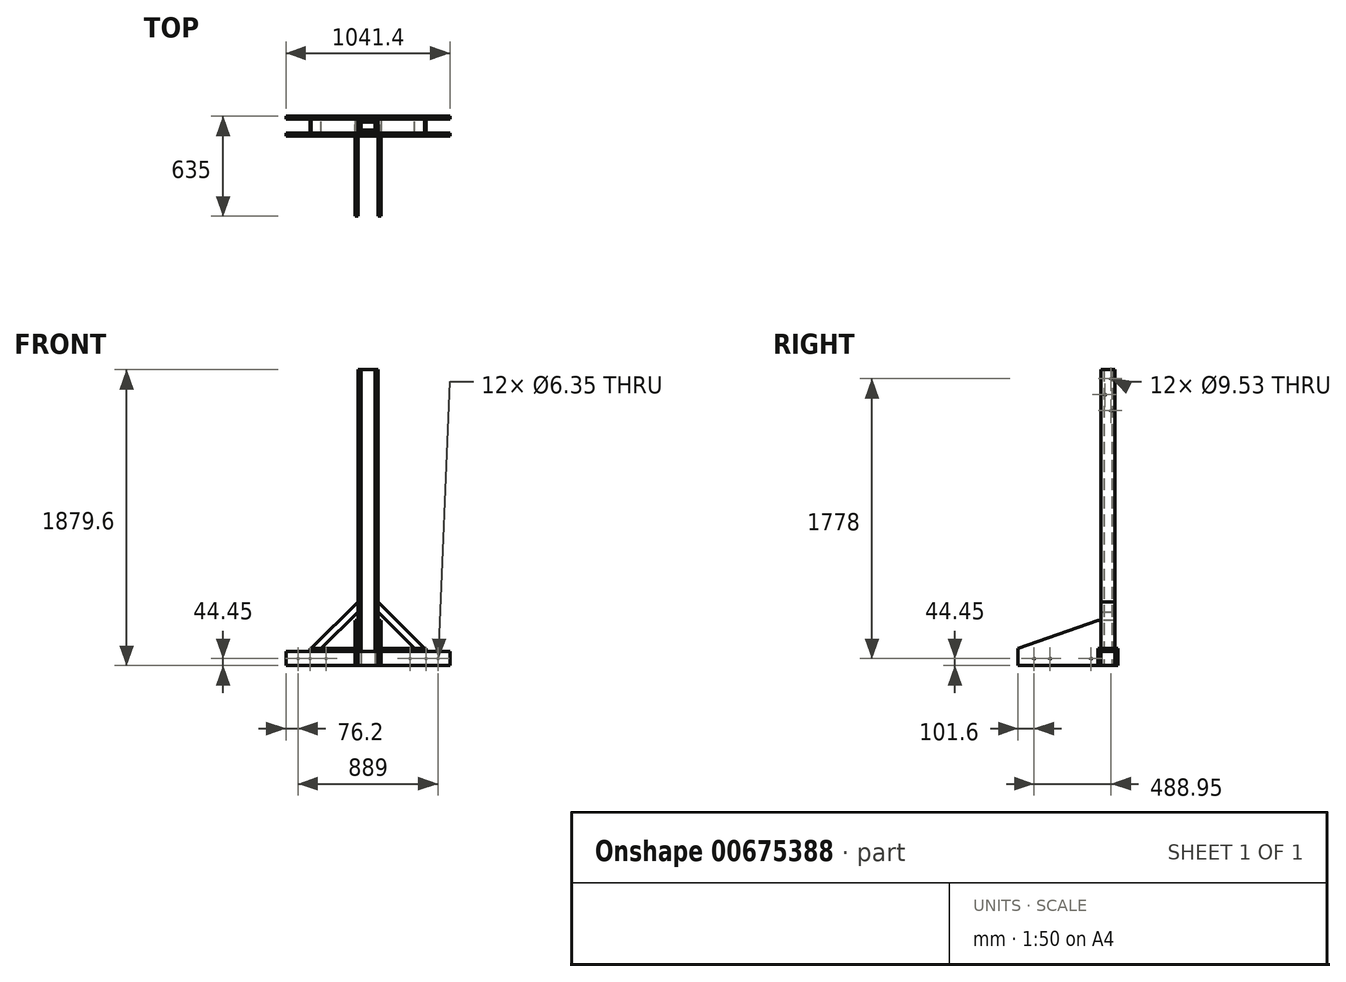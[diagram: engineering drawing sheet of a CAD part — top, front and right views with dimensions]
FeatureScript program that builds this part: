
annotation { "Feature Type Name" : "Feature", "Feature Type Description" : "" }
export const myFeature = defineFeature(function(context is Context, id is Id, definition is map)
    precondition{}
    {
        {
            var Q0;
            Q0=qCreatedBy(makeId("Top.planeOp"),FACE);
            var sketch = newSketch(context, id + "F0", { "sketchPlane" : qUnion([Q0])});
            skLineSegment(sketch, "E0.bottom", {"start": v(-44.45, 25.4) * mm, "end": v(44.45, 25.4) * mm});
            skLineSegment(sketch, "E0.top", {"start": v(-44.45, 44.45) * mm, "end": v(44.45, 44.45) * mm});
            skLineSegment(sketch, "E0.left", {"start": v(-44.45, 25.4) * mm, "end": v(-44.45, 44.45) * mm});
            skLineSegment(sketch, "E0.right", {"start": v(44.45, 25.4) * mm, "end": v(44.45, 44.45) * mm});
            skLineSegment(sketch, "E1.bottom", {"start": v(-44.45, -44.45) * mm, "end": v(44.45, -44.45) * mm});
            skLineSegment(sketch, "E1.top", {"start": v(-44.45, -25.4) * mm, "end": v(44.45, -25.4) * mm});
            skLineSegment(sketch, "E1.left", {"start": v(-44.45, -44.45) * mm, "end": v(-44.45, -25.4) * mm});
            skLineSegment(sketch, "E1.right", {"start": v(44.45, -44.45) * mm, "end": v(44.45, -25.4) * mm});
            skSolve(sketch);
        }
        {
            var Q0;
            Q0 = qSketchRegion(id + "F0", true);
            extrude(context, id + "F1", {"entities" : qUnion([Q0]), "depth" : 1879.6 * mm, "offsetDistance" : 25.4 * mm});
        }
        {
            var Q0;
            Q0=qCreatedBy(makeId("Top.planeOp"),FACE);
            var sketch = newSketch(context, id + "F2", { "sketchPlane" : qUnion([Q0])});
            skLineSegment(sketch, "E2.bottom", {"start": v(44.45, 44.45) * mm, "end": v(63.5, 44.45) * mm});
            skLineSegment(sketch, "E2.top", {"start": v(44.45, -44.45) * mm, "end": v(63.5, -44.45) * mm});
            skLineSegment(sketch, "E2.left", {"start": v(44.45, 44.45) * mm, "end": v(44.45, -44.45) * mm});
            skLineSegment(sketch, "E2.right", {"start": v(63.5, 44.45) * mm, "end": v(63.5, -44.45) * mm});
            skLineSegment(sketch, "E3.bottom", {"start": v(-44.45, -44.45) * mm, "end": v(-63.5, -44.45) * mm});
            skLineSegment(sketch, "E3.top", {"start": v(-44.45, 44.45) * mm, "end": v(-63.5, 44.45) * mm});
            skLineSegment(sketch, "E3.left", {"start": v(-44.45, -44.45) * mm, "end": v(-44.45, 44.45) * mm});
            skLineSegment(sketch, "E3.right", {"start": v(-63.5, -44.45) * mm, "end": v(-63.5, 44.45) * mm});
            skSolve(sketch);
        }
        {
            var Q0;
            Q0 = qSketchRegion(id + "F2", true);
            extrude(context, id + "F3", {"entities" : qUnion([Q0]), "depth" : 1879.6 * mm, "offsetDistance" : 25.4 * mm});
        }
        {
            var Q0;
            Q0=qCreatedBy(makeId("Top.planeOp"),FACE);
            var sketch = newSketch(context, id + "F4", { "sketchPlane" : qUnion([Q0])});
            skLineSegment(sketch, "E4.bottom", {"start": v(-520.7, 44.45) * mm, "end": v(520.7, 44.45) * mm});
            skLineSegment(sketch, "E4.top", {"start": v(-520.7, 63.5) * mm, "end": v(520.7, 63.5) * mm});
            skLineSegment(sketch, "E4.left", {"start": v(-520.7, 44.45) * mm, "end": v(-520.7, 63.5) * mm});
            skLineSegment(sketch, "E4.right", {"start": v(520.7, 44.45) * mm, "end": v(520.7, 63.5) * mm});
            skLineSegment(sketch, "E5.bottom", {"start": v(-520.7, -63.5) * mm, "end": v(520.7, -63.5) * mm});
            skLineSegment(sketch, "E5.top", {"start": v(-520.7, -44.45) * mm, "end": v(520.7, -44.45) * mm});
            skLineSegment(sketch, "E5.left", {"start": v(-520.7, -63.5) * mm, "end": v(-520.7, -44.45) * mm});
            skLineSegment(sketch, "E5.right", {"start": v(520.7, -63.5) * mm, "end": v(520.7, -44.45) * mm});
            skSolve(sketch);
        }
        {
            var Q0;
            Q0 = qSketchRegion(id + "F4", true);
            extrude(context, id + "F5", {"entities" : qUnion([Q0]), "depth" : 88.9 * mm, "offsetDistance" : 25.4 * mm});
        }
        {
            var Q0;
            Q0=makeQuery(id+"F5.opExtrude","CAP_FACE",FACE,{"disambiguationData":[OSD([sQuery(id+"F4.wireOp",EDGE,"E4.bottom"),sQuery(id+"F4.wireOp",EDGE,"E4.top"),sQuery(id+"F4.wireOp",EDGE,"E4.left"),sQuery(id+"F4.wireOp",EDGE,"E4.right")])],"isStart":false});
            var sketch = newSketch(context, id + "F6", { "sketchPlane" : qUnion([Q0])});
            skLineSegment(sketch, "E6.bottom", {"start": v(-63.5, 63.5) * mm, "end": v(-368.3, 63.5) * mm});
            skLineSegment(sketch, "E6.top", {"start": v(-63.5, -63.5) * mm, "end": v(-368.3, -63.5) * mm});
            skLineSegment(sketch, "E6.left", {"start": v(-63.5, 63.5) * mm, "end": v(-63.5, -63.5) * mm});
            skLineSegment(sketch, "E6.right", {"start": v(-368.3, 63.5) * mm, "end": v(-368.3, -63.5) * mm});
            skLineSegment(sketch, "E7.bottom", {"start": v(63.5, 63.5) * mm, "end": v(368.3, 63.5) * mm});
            skLineSegment(sketch, "E7.top", {"start": v(63.5, -63.5) * mm, "end": v(368.3, -63.5) * mm});
            skLineSegment(sketch, "E7.left", {"start": v(63.5, 63.5) * mm, "end": v(63.5, -63.5) * mm});
            skLineSegment(sketch, "E7.right", {"start": v(368.3, 63.5) * mm, "end": v(368.3, -63.5) * mm});
            skSolve(sketch);
        }
        {
            var Q0;
            Q0 = qSketchRegion(id + "F6", true);
            extrude(context, id + "F7", {"entities" : qUnion([Q0]), "depth" : 19.05 * mm, "offsetDistance" : 25.4 * mm});
        }
        {
            var Q0;
            Q0=qCreatedBy(makeId("Front.planeOp"),FACE);
            var sketch = newSketch(context, id + "F8", { "sketchPlane" : qUnion([Q0])});
            skLineSegment(sketch, "E8", {"start": v(-359.85, 107.95) * mm, "end": v(-63.5, 404.3) * mm});
            skLineSegment(sketch, "E9", {"start": v(-63.5, 404.3) * mm, "end": v(-63.5, 341.44) * mm});
            skLineSegment(sketch, "E10", {"start": v(-63.5, 341.44) * mm, "end": v(-296.99, 107.95) * mm});
            skLineSegment(sketch, "E11", {"start": v(-296.99, 107.95) * mm, "end": v(-359.85, 107.95) * mm});
            skLineSegment(sketch, "E12", {"start": v(63.5, 404.3) * mm, "end": v(63.5, 341.44) * mm});
            skLineSegment(sketch, "E13", {"start": v(63.5, 341.44) * mm, "end": v(296.99, 107.95) * mm});
            skLineSegment(sketch, "E14", {"start": v(296.99, 107.95) * mm, "end": v(359.85, 107.95) * mm});
            skLineSegment(sketch, "E15", {"start": v(359.85, 107.95) * mm, "end": v(63.5, 404.3) * mm});
            skSolve(sketch);
        }
        {
            var Q0;
            Q0 = qSketchRegion(id + "F8", true);
            extrude(context, id + "F9", {"entities" : qUnion([Q0]), "depth" : 44.45 * mm, "offsetDistance" : 25.4 * mm, "hasSecondDirection" : true, "secondDirectionOppositeDirection" : true, "secondDirectionDepth" : 44.45 * mm});
        }
        {
            var Q0;
            Q0=makeQuery(id+"F3.opExtrude","SWEPT_FACE",FACE,{"disambiguationData":[OSD([sQuery(id+"F2.wireOp",EDGE,"E3.right")])]});
            var sketch = newSketch(context, id + "F10", { "sketchPlane" : qUnion([Q0])});
            skLineSegment(sketch, "E16", {"start": v(-44.45, 107.95) * mm, "end": v(-44.45, 285.75) * mm});
            skLineSegment(sketch, "E17", {"start": v(-44.45, 285.75) * mm, "end": v(63.5, 285.75) * mm});
            skLineSegment(sketch, "E18", {"start": v(63.5, 285.75) * mm, "end": v(571.5, 107.95) * mm});
            skLineSegment(sketch, "E19", {"start": v(571.5, 107.95) * mm, "end": v(571.5, 0) * mm});
            skLineSegment(sketch, "E20", {"start": v(571.5, 0) * mm, "end": v(63.5, 0) * mm});
            skLineSegment(sketch, "E21", {"start": v(63.5, 0) * mm, "end": v(63.5, 107.95) * mm});
            skLineSegment(sketch, "E22", {"start": v(63.5, 107.95) * mm, "end": v(-44.45, 107.95) * mm});
            skSolve(sketch);
        }
        {
            var Q0;
            Q0 = qSketchRegion(id + "F10", true);
            extrude(context, id + "F11", {"entities" : qUnion([Q0]), "depth" : 19.05 * mm, "offsetDistance" : 25.4 * mm});
        }
        {
            var Q0;
            Q0=makeQuery(id+"F3.opExtrude","SWEPT_FACE",FACE,{"disambiguationData":[OSD([sQuery(id+"F2.wireOp",EDGE,"E2.right")])]});
            var sketch = newSketch(context, id + "F12", { "sketchPlane" : qUnion([Q0])});
            skLineSegment(sketch, "E23", {"start": v(-63.5, 107.95) * mm, "end": v(44.45, 107.95) * mm});
            skLineSegment(sketch, "E24", {"start": v(44.45, 107.95) * mm, "end": v(44.45, 285.75) * mm});
            skLineSegment(sketch, "E25", {"start": v(44.45, 285.75) * mm, "end": v(-63.5, 285.75) * mm});
            skLineSegment(sketch, "E26", {"start": v(-63.5, 285.75) * mm, "end": v(-571.5, 107.95) * mm});
            skLineSegment(sketch, "E27", {"start": v(-571.5, 107.95) * mm, "end": v(-571.5, 0) * mm});
            skLineSegment(sketch, "E28", {"start": v(-571.5, 0) * mm, "end": v(-63.5, 0) * mm});
            skLineSegment(sketch, "E29", {"start": v(-63.5, 0) * mm, "end": v(-63.5, 107.95) * mm});
            skSolve(sketch);
        }
        {
            var Q0;
            Q0 = qSketchRegion(id + "F12", true);
            extrude(context, id + "F13", {"entities" : qUnion([Q0]), "depth" : 19.05 * mm, "offsetDistance" : 25.4 * mm});
        }
        {
            var Q0;
            Q0=makeQuery(id+"F5.opExtrude","SWEPT_FACE",FACE,{"disambiguationData":[OSD([sQuery(id+"F4.wireOp",EDGE,"E5.bottom")])]});
            var sketch = newSketch(context, id + "F14", { "sketchPlane" : qUnion([Q0])});
            skCircle(sketch, "E30", {"center": v(266.7, 44.45) * mm, "radius": 3.18 * mm});
            skCircle(sketch, "E31", {"center": v(368.3, 44.45) * mm, "radius": 3.18 * mm});
            skCircle(sketch, "E32", {"center": v(444.5, 44.45) * mm, "radius": 3.18 * mm});
            skCircle(sketch, "E33", {"center": v(-444.5, 44.45) * mm, "radius": 3.18 * mm});
            skCircle(sketch, "E34", {"center": v(-368.3, 44.45) * mm, "radius": 3.18 * mm});
            skCircle(sketch, "E35", {"center": v(-266.7, 44.45) * mm, "radius": 3.18 * mm});
            skSolve(sketch);
        }
        {
            var Q0;
            Q0 = qSketchRegion(id + "F14", true);
            extrude(context, id + "F15", {"entities" : qUnion([Q0]), "operationType" : NewBodyOperationType.REMOVE, "endBound" : BoundingType.THROUGH_ALL, "oppositeDirection" : true, "depth" : 254 * mm, "offsetDistance" : 25.4 * mm});
        }
        {
            var Q0;
            Q0=makeQuery(id+"F5.opExtrude","SWEPT_FACE",FACE,{"disambiguationData":[OSD([sQuery(id+"F4.wireOp",EDGE,"E4.top")])]});
            var sketch = newSketch(context, id + "F16", { "sketchPlane" : qUnion([Q0])});
            skCircle(sketch, "E36", {"center": v(-444.5, 44.45) * mm, "radius": 3.17 * mm});
            skCircle(sketch, "E37", {"center": v(-368.3, 44.45) * mm, "radius": 3.17 * mm});
            skCircle(sketch, "E38", {"center": v(-266.7, 44.45) * mm, "radius": 3.17 * mm});
            skCircle(sketch, "E39", {"center": v(266.7, 44.45) * mm, "radius": 3.17 * mm});
            skCircle(sketch, "E40", {"center": v(368.3, 44.45) * mm, "radius": 3.17 * mm});
            skCircle(sketch, "E41", {"center": v(444.5, 44.45) * mm, "radius": 3.17 * mm});
            skSolve(sketch);
        }
        {
            var Q0;
            Q0 = qSketchRegion(id + "F16", true);
            extrude(context, id + "F17", {"entities" : qUnion([Q0]), "operationType" : NewBodyOperationType.REMOVE, "endBound" : BoundingType.THROUGH_ALL, "oppositeDirection" : true, "depth" : 25.4 * mm, "offsetDistance" : 25.4 * mm});
        }
        {
            var Q0;
            Q0=makeQuery(id+"F13.opExtrude","CAP_FACE",FACE,{"disambiguationData":[OSD([sQuery(id+"F12.wireOp",EDGE,"E23"),sQuery(id+"F12.wireOp",EDGE,"E24"),sQuery(id+"F12.wireOp",EDGE,"E25"),sQuery(id+"F12.wireOp",EDGE,"E26"),sQuery(id+"F12.wireOp",EDGE,"E27"),sQuery(id+"F12.wireOp",EDGE,"E28"),sQuery(id+"F12.wireOp",EDGE,"E29")])],"isStart":false});
            var sketch = newSketch(context, id + "F18", { "sketchPlane" : qUnion([Q0])});
            skCircle(sketch, "E42", {"center": v(-107.95, 44.45) * mm, "radius": 4.76 * mm});
            skCircle(sketch, "E43", {"center": v(-368.3, 44.45) * mm, "radius": 4.76 * mm});
            skCircle(sketch, "E44", {"center": v(-469.9, 44.45) * mm, "radius": 4.76 * mm});
            skSolve(sketch);
        }
        {
            var Q0;
            Q0 = qSketchRegion(id + "F18", true);
            extrude(context, id + "F19", {"entities" : qUnion([Q0]), "operationType" : NewBodyOperationType.REMOVE, "endBound" : BoundingType.THROUGH_ALL, "oppositeDirection" : true, "depth" : 25.4 * mm, "offsetDistance" : 25.4 * mm});
        }
        {
            var Q0;
            Q0=makeQuery(id+"F11.opExtrude","CAP_FACE",FACE,{"disambiguationData":[OSD([sQuery(id+"F10.wireOp",EDGE,"E16"),sQuery(id+"F10.wireOp",EDGE,"E17"),sQuery(id+"F10.wireOp",EDGE,"E18"),sQuery(id+"F10.wireOp",EDGE,"E19"),sQuery(id+"F10.wireOp",EDGE,"E20"),sQuery(id+"F10.wireOp",EDGE,"E21"),sQuery(id+"F10.wireOp",EDGE,"E22")])],"isStart":false});
            var sketch = newSketch(context, id + "F20", { "sketchPlane" : qUnion([Q0])});
            skCircle(sketch, "E45", {"center": v(107.95, 44.45) * mm, "radius": 4.76 * mm});
            skCircle(sketch, "E46", {"center": v(368.3, 44.45) * mm, "radius": 4.76 * mm});
            skCircle(sketch, "E47", {"center": v(469.9, 44.45) * mm, "radius": 4.76 * mm});
            skSolve(sketch);
        }
        {
            var Q0;
            Q0 = qSketchRegion(id + "F20", true);
            extrude(context, id + "F21", {"entities" : qUnion([Q0]), "operationType" : NewBodyOperationType.REMOVE, "oppositeDirection" : true, "depth" : 25.4 * mm, "offsetDistance" : 25.4 * mm});
        }
        {
            var Q0;
            Q0=makeQuery(id+"F3.opExtrude","SWEPT_FACE",FACE,{"disambiguationData":[OSD([sQuery(id+"F2.wireOp",EDGE,"E2.right")])]});
            var sketch = newSketch(context, id + "F22", { "sketchPlane" : qUnion([Q0])});
            skCircle(sketch, "E48", {"center": v(19.05, 1822.45) * mm, "radius": 4.76 * mm});
            skCircle(sketch, "E49", {"center": v(-19.05, 1720.85) * mm, "radius": 4.76 * mm});
            skCircle(sketch, "E50", {"center": v(19.05, 1619.25) * mm, "radius": 4.76 * mm});
            skSolve(sketch);
        }
        {
            var Q0;
            Q0 = qSketchRegion(id + "F22", true);
            extrude(context, id + "F23", {"entities" : qUnion([Q0]), "operationType" : NewBodyOperationType.REMOVE, "oppositeDirection" : true, "depth" : 25.4 * mm, "offsetDistance" : 25.4 * mm});
        }
        {
            var Q0;
            Q0=makeQuery(id+"F3.opExtrude","SWEPT_FACE",FACE,{"disambiguationData":[OSD([sQuery(id+"F2.wireOp",EDGE,"E3.right")])]});
            var sketch = newSketch(context, id + "F24", { "sketchPlane" : qUnion([Q0])});
            skCircle(sketch, "E51", {"center": v(-19.05, 1822.45) * mm, "radius": 4.76 * mm});
            skCircle(sketch, "E52", {"center": v(19.05, 1720.85) * mm, "radius": 4.76 * mm});
            skCircle(sketch, "E53", {"center": v(-19.05, 1619.25) * mm, "radius": 4.76 * mm});
            skSolve(sketch);
        }
        {
            var Q0;
            Q0 = qSketchRegion(id + "F24", true);
            extrude(context, id + "F25", {"entities" : qUnion([Q0]), "operationType" : NewBodyOperationType.REMOVE, "oppositeDirection" : true, "depth" : 25.4 * mm, "offsetDistance" : 25.4 * mm});
        }
    });
